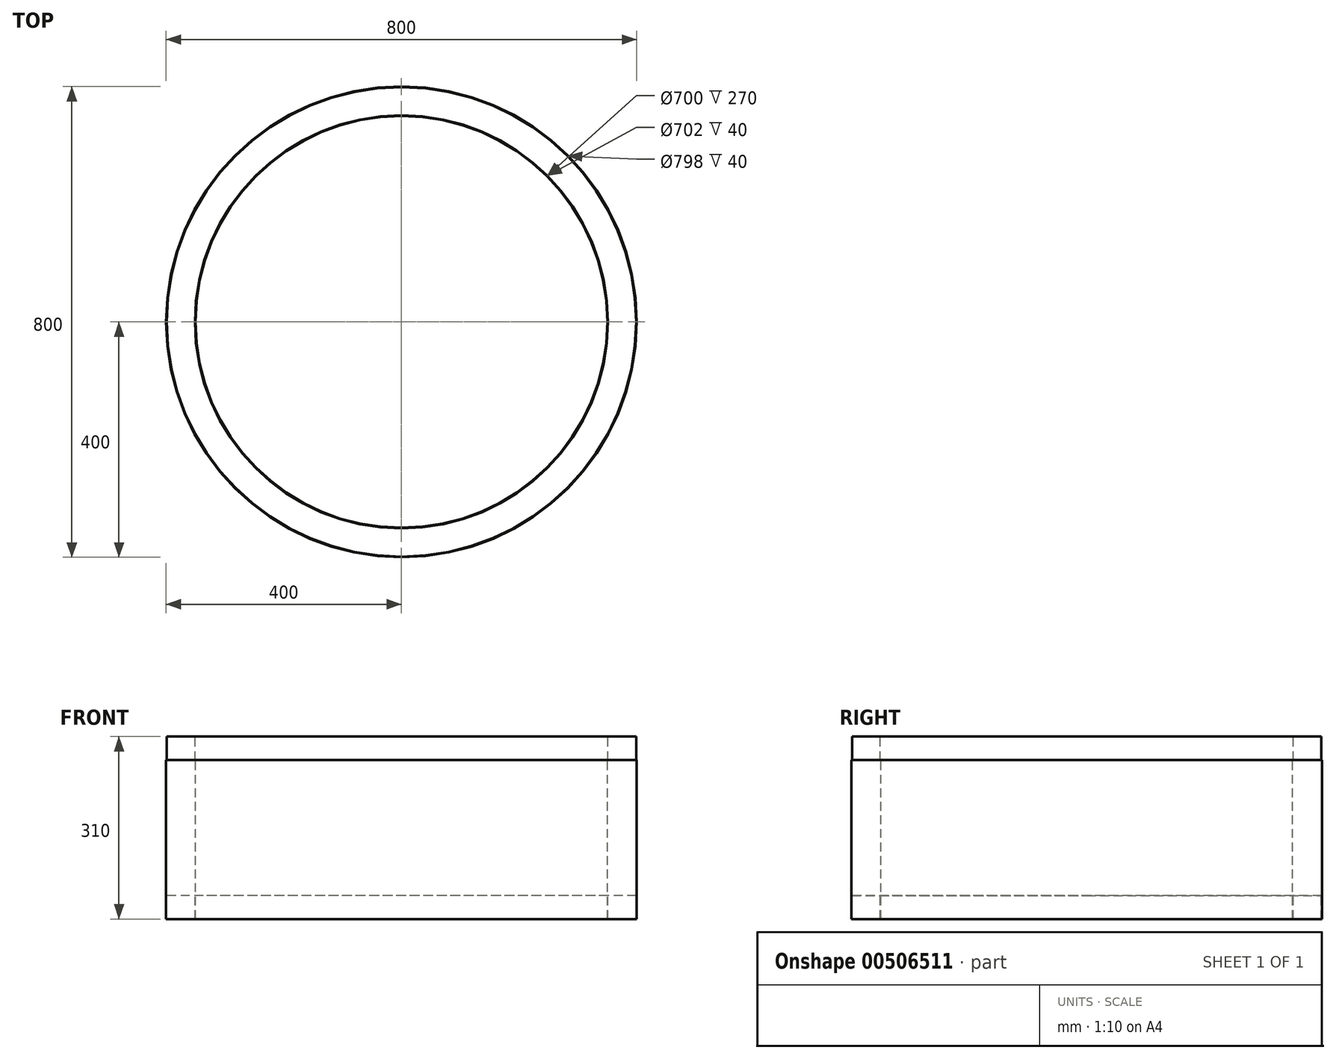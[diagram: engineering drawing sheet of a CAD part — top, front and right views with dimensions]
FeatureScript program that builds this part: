
annotation { "Feature Type Name" : "Feature", "Feature Type Description" : "" }
export const myFeature = defineFeature(function(context is Context, id is Id, definition is map)
    precondition{}
    {
        {
            var Q0;
            Q0=qCreatedBy(makeId("Front.planeOp"),FACE);
            var sketch = newSketch(context, id + "F0", { "sketchPlane" : qUnion([Q0])});
            skLineSegment(sketch, "E0", {"start": v(0, 74.87) * mm, "end": v(0, -73.71) * mm, "construction": true});
            skLineSegment(sketch, "E1", {"start": v(0, 374.84) * mm, "end": v(0, -528.94) * mm, "construction": true});
            skLineSegment(sketch, "E2", {"start": v(-350, -489.75) * mm, "end": v(-350, -219.75) * mm});
            skLineSegment(sketch, "E3", {"start": v(-350, -219.75) * mm, "end": v(-351, -219.75) * mm});
            skLineSegment(sketch, "E4", {"start": v(-351, -219.75) * mm, "end": v(-351, -179.75) * mm});
            skLineSegment(sketch, "E5", {"start": v(-351, -179.75) * mm, "end": v(-399, -179.75) * mm});
            skLineSegment(sketch, "E6", {"start": v(-399, -179.75) * mm, "end": v(-399, -219.75) * mm});
            skLineSegment(sketch, "E7", {"start": v(-399, -219.75) * mm, "end": v(-400, -219.75) * mm});
            skLineSegment(sketch, "E8", {"start": v(-400, -219.75) * mm, "end": v(-400, -489.75) * mm});
            skLineSegment(sketch, "E9", {"start": v(-400, -489.75) * mm, "end": v(-399, -489.75) * mm});
            skLineSegment(sketch, "E10", {"start": v(-399, -489.75) * mm, "end": v(-399, -449.75) * mm});
            skLineSegment(sketch, "E11", {"start": v(-399, -449.75) * mm, "end": v(-351, -449.75) * mm});
            skLineSegment(sketch, "E12", {"start": v(-351, -449.75) * mm, "end": v(-351, -489.75) * mm});
            skLineSegment(sketch, "E13", {"start": v(-351, -489.75) * mm, "end": v(-350, -489.75) * mm});
            skSolve(sketch);
        }
        {
            var Q0;
            Q0=qSketchRegion(id+"F0",true);
            var Q1;
            Q1=sQuery(id+"F0.wireOp",EDGE,"E1");
            revolve(context, id + "F1", {"entities" : qUnion([Q0]), "axis" : qUnion([Q1]), "revolveType" : RevolveType.FULL});
        }
    });
